# Revit family: Boiler-Gas-Weil-McLain-80_Boiler-BG580WF
name_source: partatom
category: Mechanical Equipment
units: mm (PartAtom-declared; Revit-internal decimal feet)

## family parameters
Always vertical = Yes
Cut with Voids When Loaded = No
OmniClass Number = 23.75.10.11.14.11
OmniClass Title = Cast-Iron Boilers
Part Type = Normal
Room Calculation Point = No
Round Connector Dimension = Use Radius
Shared = No
Work Plane-Based = No

## types (10) — shared parameters
Apparent Load = 249 VA
Casing = Metal - Weil-McLain - Paint Grey
Combustion Efficiency = 82.6%
Default Elevation = 0"
Description = 80 Commercial Gas Oil Boiler
Frequency = 60 Hz
Gas Flow = 0.16
Gas Pressure Drop = 0.05 psi
Manufacturer = WEIL-McLAIN
Model = BG580WF
Number of Poles = 1
Phase = 1
Power Factor = 1
Product Documentation Link = http://www.weil-mclain.com
Product Name = 80 BOILER
Product Page URL = http://www.weil-mclain.com
Return Connection Diameter = 3"
Return Connection Radius = 1 1/2"
Shipping Weight = 1875.00 lb
Supply Connection Diameter = 4"
Supply Connection Radius = 2"
Thermal Efficiency = 80.6%
URL = http://www.weil-mclain.com
Voltage = 120 V
Water Connection Diameter = 1"
Water Connection Radius = 1/2"
Width = 2' - 5 7/8"

## per-type parameters (varying)
| type | A | Actual Exhaust Air Flow | B | Boiler Horsepower | Exhaust Connection Radius | Exhaust Pipe Diameter | Flue B | Gas Connection Diameter | Gas Connection Radius | Gas Net I=B=R | Gross I=B=R Rating | Length | Net I=B=R Rating |
| 380 | 1' - 1 1/8" | 139 CFM | 0" | 8.3 | 4" | 8" | No | 1 1/4" | 5/8" | 346000.0 Btu/h | 278000.0 Btu/h | 1' - 9 5/8" | 242000.0 Btu/h |
| 480 | 1' - 8 1/8" | 198 CFM | 0" | 11.8 | 4" | 8" | No | 1 1/4" | 5/8" | 491000.0 Btu/h | 396000.0 Btu/h | 2' - 4 5/8" | 344000.0 Btu/h |
| 580 | 2' - 3 1/8" | 259 CFM | 0" | 15.4 | 4" | 8" | No | 1 1/4" | 5/8" | 639000.0 Btu/h | 515000.0 Btu/h | 2' - 11 5/8" | 448000.0 Btu/h |
| 680 | 2' - 10 1/8" | 320 CFM | 0" | 18.9 | 4" | 8" | No | 1 1/4" | 5/8" | 787000.0 Btu/h | 634000.0 Btu/h | 3' - 6 5/8" | 551000.0 Btu/h |
| 780 | 3' - 5 1/8" | 378 CFM | 0" | 22.5 | 5" | 10" | No | 1 1/4" | 5/8" | 935000.0 Btu/h | 753000.0 Btu/h | 4' - 1 5/8" | 655000.0 Btu/h |
| 880 | 4' - 0 1/8" | 436 CFM | 0" | 26 | 5" | 10" | No | 1 1/4" | 5/8" | 1082000.0 Btu/h | 872000.0 Btu/h | 4' - 8 5/8" | 758000.0 Btu/h |
| 980 | 4' - 7 1/8" | 494 CFM | 0" | 29.6 | 5" | 10" | No | 1 1/4" | 5/8" | 1230000.0 Btu/h | 991000.0 Btu/h | 5' - 3 5/8" | 862000.0 Btu/h |
| 1080 | 5' - 2 1/8" | 558 CFM | 2' - 3 9/16" | 33.2 | 5" | 10" | Yes | 1 1/4" | 5/8" | 1378000.0 Btu/h | 1110000.0 Btu/h | 5' - 10 5/8" | 965000.0 Btu/h |
| 1180 | 5' - 9 1/8" | 616 CFM | 2' - 10 9/16" | 36.7 | 5" | 10" | Yes | 2" | 1" | 1526000.0 Btu/h | 1229000.0 Btu/h | 6' - 5 5/8" | 1069000.0 Btu/h |
| 1280 | 6' - 4 1/8" | 675 CFM | 2' - 10 9/16" | 40.3 | 6" | 1' - 0" | Yes | 2" | 1" | 1674000.0 Btu/h | 1348000.0 Btu/h | 7' - 0 5/8" | 1172000.0 Btu/h |

note: source unit labels omitted for Gas Flow — the stored unit's dimension contradicts the parameter name (converter mislabeling)

## geometry (parser evidence)
native form markers: Blend x6, Sweep x6
no freeform markers — native parametric forms only
